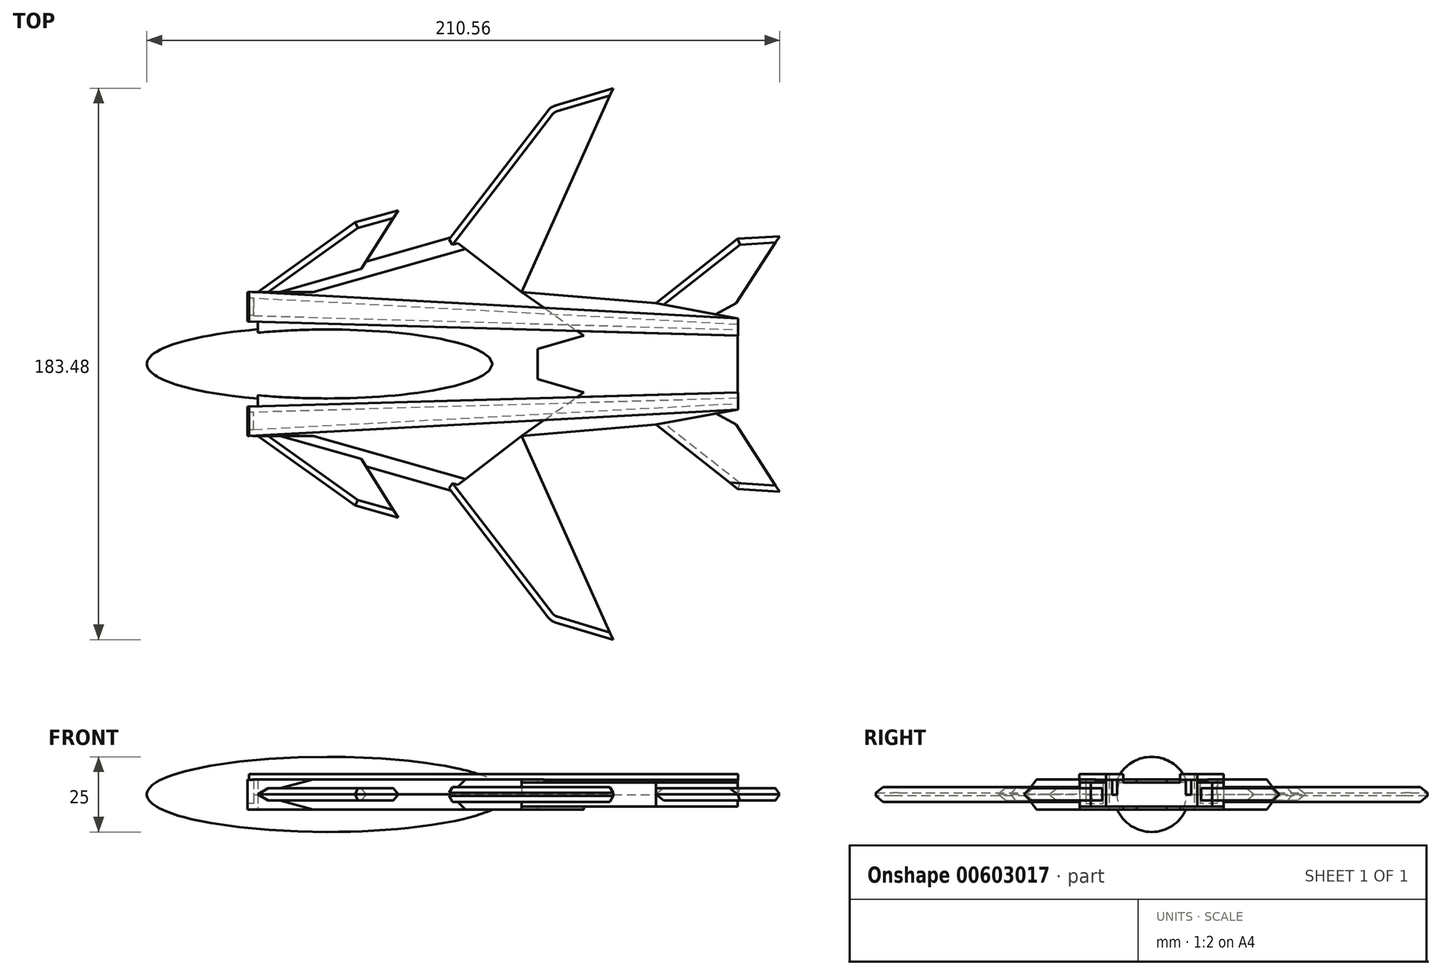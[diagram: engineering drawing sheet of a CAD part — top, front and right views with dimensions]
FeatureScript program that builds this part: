
annotation { "Feature Type Name" : "Feature", "Feature Type Description" : "" }
export const myFeature = defineFeature(function(context is Context, id is Id, definition is map)
    precondition{}
    {
        {
            var Q0;
            Q0=qCreatedBy(makeId("Top.planeOp"),FACE);
            var sketch = newSketch(context, id + "F0", { "sketchPlane" : qUnion([Q0])});
            skEllipticalArc(sketch, "E0", {});
            skLineSegment(sketch, "E1", {"start": v(0, 12.5) * mm, "end": v(0, -12.5) * mm});
            skLineSegment(sketch, "E2", {"start": v(0, 0) * mm, "end": v(-60, 0) * mm});
            const initialGuessF0  = {"E0": [0, 0, 1, 0, 0.06, 0.0125, 3.141592653589793, 4.71238898038469]};
            skSetInitialGuess(sketch, initialGuessF0);
            skSolve(sketch);
        }
        {
            var Q0;
            Q0=qCreatedBy(makeId("Right.planeOp"),FACE);
            var sketch = newSketch(context, id + "F1", { "sketchPlane" : qUnion([Q0])});
            skPoint(sketch, "E3.0", {"position": v(0, 0) * mm});
            skLineSegment(sketch, "E4", {"start": v(0, 0) * mm, "end": v(-12.5, 0) * mm});
            skCircle(sketch, "E5", {"center": v(0, 0) * mm, "radius": 12.5 * mm});
            skSolve(sketch);
        }
        {
            var Q0;
            {var subQ0=sQuery(id+"F0.wireOp",EDGE,"E0");Q0=makeQuery(id+"F0.imprint","IMPRINT",FACE,{"disambiguationData":[TD([[makeQuery(id+"F0.imprint","IMPRINT",EDGE,{"derivedFrom":subQ0}),1.0]])]});}
            var Q1;
            Q1=sQuery(id+"F1.wireOp",EDGE,"E5");
            sweep(context, id + "F2", {"profiles" : qUnion([Q0]), "path" : qUnion([Q1])});
        }
        {
            var Q0;
            Q0=makeQuery(id+"F2.opSweep","SWEPT_BODY",BODY,{"disambiguationData":[OSD([sQuery(id+"F0.wireOp",EDGE,"E0"),sQuery(id+"F0.wireOp",EDGE,"E1"),sQuery(id+"F0.wireOp",EDGE,"E2"),sQuery(id+"F1.wireOp",EDGE,"E5")])]});
            var Q1;
            Q1=qCreatedBy(makeId("Right.planeOp"),FACE);
            mirror(context, id + "F3", {"operationType" : NewBodyOperationType.ADD, "entities" : qUnion([Q0]), "mirrorPlane" : qUnion([Q1])});
        }
        {
            var Q0;
            Q0=qCreatedBy(makeId("Top.planeOp"),FACE);
            var sketch = newSketch(context, id + "F4", { "sketchPlane" : qUnion([Q0])});
            skEllipticalArc(sketch, "E6.0", {});
            skLineSegment(sketch, "E7", {"start": v(-23.05, -11.54) * mm, "end": v(-23.05, -14.14) * mm});
            skLineSegment(sketch, "E8", {"start": v(-23.05, -14.14) * mm, "end": v(-26.5, -14.14) * mm});
            skLineSegment(sketch, "E9", {"start": v(-26.5, -14.14) * mm, "end": v(-26.5, -23.94) * mm});
            skLineSegment(sketch, "E10", {"start": v(-26.5, -23.94) * mm, "end": v(-23.05, -23.94) * mm});
            skLineSegment(sketch, "E11", {"start": v(-23.05, -23.94) * mm, "end": v(41.04, -42.09) * mm});
            skLineSegment(sketch, "E12", {"start": v(41.04, -42.09) * mm, "end": v(64.69, -23.94) * mm});
            skLineSegment(sketch, "E13", {"start": v(64.69, -23.94) * mm, "end": v(85.37, -9.43) * mm});
            skLineSegment(sketch, "E14", {"start": v(85.37, -9.43) * mm, "end": v(70, -5) * mm});
            skLineSegment(sketch, "E15", {"start": v(70, -5) * mm, "end": v(70, 0) * mm});
            skLineSegment(sketch, "E16", {"start": v(-23.05, -23.94) * mm, "end": v(9.37, -47.1) * mm});
            skLineSegment(sketch, "E17", {"start": v(9.37, -47.1) * mm, "end": v(23.65, -51.15) * mm});
            skLineSegment(sketch, "E18", {"start": v(23.65, -51.15) * mm, "end": v(12.96, -34.14) * mm});
            skLineSegment(sketch, "E19", {"start": v(64.69, -23.94) * mm, "end": v(109.34, -20.2) * mm});
            skLineSegment(sketch, "E20", {"start": v(109.34, -20.2) * mm, "end": v(136.64, -15.13) * mm});
            skLineSegment(sketch, "E21", {"start": v(136.64, -15.13) * mm, "end": v(136.64, 0) * mm});
            skLineSegment(sketch, "E22", {"start": v(136.64, 0) * mm, "end": v(70, 0) * mm});
            skLineSegment(sketch, "E23", {"start": v(109.34, -20.2) * mm, "end": v(136.64, -41.65) * mm});
            skLineSegment(sketch, "E24", {"start": v(136.64, -41.65) * mm, "end": v(150.56, -42.52) * mm});
            skLineSegment(sketch, "E25", {"start": v(150.56, -42.52) * mm, "end": v(136.06, -20.2) * mm});
            skLineSegment(sketch, "E26", {"start": v(136.06, -20.2) * mm, "end": v(129.3, -16.5) * mm});
            skLineSegment(sketch, "E27", {"start": v(-23.05, -11.54) * mm, "end": v(-23.05, 0) * mm});
            skLineSegment(sketch, "E28", {"start": v(-23.05, 0) * mm, "end": v(70, 0) * mm});
            skLineSegment(sketch, "E29", {"start": v(41.04, -42.09) * mm, "end": v(73.42, -84.26) * mm});
            skLineSegment(sketch, "E30", {"start": v(75.95, -86) * mm, "end": v(95.11, -91.74) * mm});
            skLineSegment(sketch, "E31", {"start": v(95.11, -91.74) * mm, "end": v(64.69, -23.94) * mm});
            skPoint(sketch, "E32.visualSharp", {"position": v(74.4, -85.54) * mm});
            skArc(sketch, "E32.filletArc", {"start": v(73.42, -84.26) * mm, "mid": v(74.55, -85.33) * mm, "end": v(75.95, -86) * mm});
            const initialGuessF4  = {"E6.0": [0, 0, 1, 0, 0.06, 0.0125, 3.141592653589793, 4.71238898038469]};
            skSetInitialGuess(sketch, initialGuessF4);
            skSolve(sketch);
        }
        {
            var Q0;
            Q0=makeQuery(id+"F4.imprint","IMPRINT",FACE,{"disambiguationData":[TD([[makeQuery(id+"F4.imprint","IMPRINT",EDGE,{"derivedFrom":sQuery(id+"F4.wireOp",EDGE,"E7")}),1.0]])]});
            extrude(context, id + "F5", {"entities" : qUnion([Q0]), "operationType" : NewBodyOperationType.ADD, "endBound" : BoundingType.SYMMETRIC, "depth" : 10 * mm, "offsetDistance" : 25 * mm});
        }
        {
            var Q0;
            Q0=makeQuery(id+"F4.imprint","IMPRINT",FACE,{"disambiguationData":[TD([[makeQuery(id+"F4.imprint","IMPRINT",EDGE,{"derivedFrom":sQuery(id+"F4.wireOp",EDGE,"E13")}),-1.0]])]});
            extrude(context, id + "F6", {"entities" : qUnion([Q0]), "operationType" : NewBodyOperationType.ADD, "endBound" : BoundingType.SYMMETRIC, "depth" : 8 * mm, "offsetDistance" : 25 * mm});
        }
        {
            var Q0;
            {var subQ0=sQuery(id+"F4.wireOp",EDGE,"E16");Q0=makeQuery(id+"F4.imprint","IMPRINT",FACE,{"disambiguationData":[TD([[makeQuery(id+"F4.imprint","IMPRINT",EDGE,{"derivedFrom":subQ0}),1.0]])]});}
            var Q1;
            {var subQ0=sQuery(id+"F4.wireOp",EDGE,"E23");Q1=makeQuery(id+"F4.imprint","IMPRINT",FACE,{"disambiguationData":[TD([[makeQuery(id+"F4.imprint","IMPRINT",EDGE,{"derivedFrom":subQ0}),1.0]])]});}
            extrude(context, id + "F7", {"entities" : qUnion([Q0, Q1]), "operationType" : NewBodyOperationType.ADD, "endBound" : BoundingType.SYMMETRIC, "depth" : 4 * mm, "offsetDistance" : 25 * mm});
        }
        {
            var Q0;
            Q0=makeQuery(id+"F5.opExtrude","CAP_FACE",FACE,{"disambiguationData":[OSD([sQuery(id+"F4.wireOp",EDGE,"E7"),sQuery(id+"F4.wireOp",EDGE,"E8"),sQuery(id+"F4.wireOp",EDGE,"E9"),sQuery(id+"F4.wireOp",EDGE,"E10"),sQuery(id+"F4.wireOp",EDGE,"E11"),sQuery(id+"F4.wireOp",EDGE,"E12"),sQuery(id+"F4.wireOp",EDGE,"E13"),sQuery(id+"F4.wireOp",EDGE,"E14"),sQuery(id+"F4.wireOp",EDGE,"E15"),sQuery(id+"F4.wireOp",EDGE,"E27"),sQuery(id+"F4.wireOp",EDGE,"E28")])],"isStart":false});
            var sketch = newSketch(context, id + "F8", { "sketchPlane" : qUnion([Q0])});
            skLineSegment(sketch, "E33.0.0", {"start": v(136.64, -15.13) * mm, "end": v(136.64, 0) * mm});
            skLineSegment(sketch, "E33.0.1", {"start": v(136.64, 0) * mm, "end": v(70, 0) * mm});
            skLineSegment(sketch, "E33.0.2", {"start": v(70, 0) * mm, "end": v(70, -5) * mm});
            skLineSegment(sketch, "E33.0.3", {"start": v(70, -5) * mm, "end": v(85.37, -9.43) * mm});
            skLineSegment(sketch, "E33.0.4", {"start": v(85.37, -9.43) * mm, "end": v(64.69, -23.94) * mm});
            skLineSegment(sketch, "E33.0.5", {"start": v(64.69, -23.94) * mm, "end": v(109.34, -20.2) * mm});
            skLineSegment(sketch, "E33.0.6", {"start": v(109.34, -20.2) * mm, "end": v(136.64, -15.13) * mm});
            skLineSegment(sketch, "E34", {"start": v(136.64, -15.13) * mm, "end": v(-26.5, -23.94) * mm});
            skLineSegment(sketch, "E35", {"start": v(-26.5, -23.94) * mm, "end": v(-26.5, -14.14) * mm});
            skLineSegment(sketch, "E36", {"start": v(-26.5, -14.14) * mm, "end": v(136.64, -9.43) * mm});
            skLineSegment(sketch, "E37", {"start": v(136.64, -9.43) * mm, "end": v(136.64, -15.13) * mm});
            skLineSegment(sketch, "E38.0", {"start": v(-24.5, -16.08) * mm, "end": v(136.64, -11.44) * mm});
            skLineSegment(sketch, "E38.1", {"start": v(-24.5, -21.83) * mm, "end": v(-24.5, -16.08) * mm});
            skLineSegment(sketch, "E38.2", {"start": v(136.64, -13.13) * mm, "end": v(-24.5, -21.83) * mm});
            skSolve(sketch);
        }
        {
            var Q0;
            {var subQ0=sQuery(id+"F8.wireOp",EDGE,"E35");Q0=makeQuery(id+"F8.imprint","IMPRINT",FACE,{"disambiguationData":[TD([[makeQuery(id+"F8.imprint","IMPRINT",EDGE,{"derivedFrom":subQ0}),1.0]])]});}
            var Q1;
            {var subQ0=sQuery(id+"F8.wireOp",EDGE,"E34");var subQ1=sQuery(id+"F8.wireOp",EDGE,"E33.0.4");var subQ2=makeQuery(id+"F8.imprint","INTERSECT",VERTEX,{"derivedFrom":[subQ1,subQ0]});Q1=makeQuery(id+"F8.imprint","IMPRINT",FACE,{"disambiguationData":[TD([[makeQuery(id+"F8.imprint","IMPRINT",EDGE,{"disambiguationData":[TD([[subQ2,-1.0]])],"derivedFrom":subQ1}),-1.0]])]});}
            var Q2;
            {var subQ0=sQuery(id+"F8.wireOp",EDGE,"E38.0");var subQ1=sQuery(id+"F8.wireOp",EDGE,"E33.0.4");var subQ2=makeQuery(id+"F8.imprint","INTERSECT",VERTEX,{"derivedFrom":[subQ1,subQ0]});Q2=makeQuery(id+"F8.imprint","IMPRINT",FACE,{"disambiguationData":[TD([[makeQuery(id+"F8.imprint","IMPRINT",EDGE,{"disambiguationData":[TD([[subQ2,-1.0]])],"derivedFrom":subQ1}),-1.0]])]});}
            extrude(context, id + "F9", {"entities" : qUnion([Q0, Q1, Q2]), "operationType" : NewBodyOperationType.ADD, "oppositeDirection" : true, "depth" : 4 * mm, "offsetDistance" : 25 * mm});
        }
        {
            var Q0;
            {var subQ5=sQuery(id+"F8.wireOp",EDGE,"E38.1");Q0=makeQuery(id+"F8.imprint","IMPRINT",FACE,{"disambiguationData":[TD([[makeQuery(id+"F8.imprint","IMPRINT",EDGE,{"derivedFrom":subQ5}),-1.0]])]});}
            var Q1;
            {var subQ0=sQuery(id+"F8.wireOp",EDGE,"E38.2");var subQ1=sQuery(id+"F8.wireOp",EDGE,"E33.0.4");var subQ2=makeQuery(id+"F8.imprint","INTERSECT",VERTEX,{"derivedFrom":[subQ1,subQ0]});Q1=makeQuery(id+"F8.imprint","IMPRINT",FACE,{"disambiguationData":[TD([[makeQuery(id+"F8.imprint","IMPRINT",EDGE,{"disambiguationData":[TD([[subQ2,-1.0]])],"derivedFrom":subQ1}),-1.0]])]});}
            extrude(context, id + "F10", {"entities" : qUnion([Q0, Q1]), "operationType" : NewBodyOperationType.REMOVE, "oppositeDirection" : true, "depth" : 5.1 * mm, "offsetDistance" : 25 * mm});
        }
        {
            var Q0;
            Q0=makeQuery(id+"F5.opExtrude","SWEPT_FACE",FACE,{"disambiguationData":[OSD([sQuery(id+"F4.wireOp",EDGE,"E9")])]});
            var sketch = newSketch(context, id + "F11", { "sketchPlane" : qUnion([Q0])});
            skLineSegment(sketch, "E39.bottom", {"start": v(21.94, 5) * mm, "end": v(16.14, 5) * mm});
            skLineSegment(sketch, "E39.top", {"start": v(21.94, -3) * mm, "end": v(16.14, -3) * mm});
            skLineSegment(sketch, "E39.left", {"start": v(21.94, 5) * mm, "end": v(21.94, -3) * mm});
            skLineSegment(sketch, "E39.right", {"start": v(16.14, 5) * mm, "end": v(16.14, -3) * mm});
            skLineSegment(sketch, "E40.bottom", {"start": v(16.14, -3) * mm, "end": v(16.14, -3) * mm});
            skSolve(sketch);
        }
        {
            var Q0;
            Q0=qCreatedBy(makeId("Top.planeOp"),FACE);
            cPlane(context, id + "F12", {"entities" : qUnion([Q0]), "cplaneType" : CPlaneType.OFFSET, "offset" : 4.8 * mm, "width" : 150 * mm, "height" : 150 * mm});
        }
        {
            var Q0;
            Q0=qCreatedBy(id+"F12.planeOp",FACE);
            var sketch = newSketch(context, id + "F13", { "sketchPlane" : qUnion([Q0])});
            skLineSegment(sketch, "E41", {"start": v(-26, -14.12) * mm, "end": v(-26, -24) * mm});
            skLineSegment(sketch, "E42", {"start": v(-26, -24) * mm, "end": v(136.68, -15.15) * mm});
            skLineSegment(sketch, "E43", {"start": v(136.68, -15.15) * mm, "end": v(136.68, -9.47) * mm});
            skLineSegment(sketch, "E44", {"start": v(136.68, -9.47) * mm, "end": v(-26, -14.12) * mm});
            skSolve(sketch);
        }
        {
            var Q0;
            Q0 = qSketchRegion(id + "F13", true);
            var Q1;
            Q1=makeQuery(id+"F13.imprint","IMPRINT",FACE,{"disambiguationData":[TD([[makeQuery(id+"F13.imprint","IMPRINT",EDGE,{"derivedFrom":sQuery(id+"F13.wireOp",EDGE,"E41")}),1.0]])]});
            extrude(context, id + "F14", {"entities" : qUnion([Q0, Q1]), "operationType" : NewBodyOperationType.ADD, "depth" : 2 * mm, "offsetDistance" : 25 * mm});
        }
        {
            var Q0;
            Q0=makeQuery(id+"F11.imprint","IMPRINT",FACE,{"disambiguationData":[TD([[makeQuery(id+"F11.imprint","IMPRINT",EDGE,{"derivedFrom":sQuery(id+"F11.wireOp",EDGE,"E39.bottom")}),-1.0]])]});
            extrude(context, id + "F15", {"entities" : qUnion([Q0]), "operationType" : NewBodyOperationType.REMOVE, "oppositeDirection" : true, "depth" : 2 * mm, "offsetDistance" : 25 * mm});
        }
        {
            var Q0;
            Q0=makeQuery(id+"F2.opSweep","SWEPT_BODY",BODY,{"disambiguationData":[OSD([sQuery(id+"F0.wireOp",EDGE,"E0"),sQuery(id+"F0.wireOp",EDGE,"E1"),sQuery(id+"F0.wireOp",EDGE,"E2"),sQuery(id+"F1.wireOp",EDGE,"E5")])]});
            var Q1;
            Q1=qCreatedBy(makeId("Front.planeOp"),FACE);
            mirror(context, id + "F16", {"operationType" : NewBodyOperationType.ADD, "entities" : qUnion([Q0]), "mirrorPlane" : qUnion([Q1])});
        }
        {
            var Q0;
            Q0=makeQuery(id+"F4.imprint","IMPRINT",FACE,{"disambiguationData":[TD([[makeQuery(id+"F4.imprint","IMPRINT",EDGE,{"derivedFrom":sQuery(id+"F4.wireOp",EDGE,"E12")}),-1.0]])]});
            extrude(context, id + "F17", {"entities" : qUnion([Q0]), "operationType" : NewBodyOperationType.ADD, "endBound" : BoundingType.SYMMETRIC, "depth" : 5 * mm, "offsetDistance" : 25 * mm});
        }
        {
            var Q0;
            Q0=makeQuery(id+"F2.opSweep","SWEPT_BODY",BODY,{"disambiguationData":[OSD([sQuery(id+"F0.wireOp",EDGE,"E0"),sQuery(id+"F0.wireOp",EDGE,"E1"),sQuery(id+"F0.wireOp",EDGE,"E2"),sQuery(id+"F1.wireOp",EDGE,"E5")])]});
            var Q1;
            Q1=qCreatedBy(makeId("Front.planeOp"),FACE);
            mirror(context, id + "F18", {"operationType" : NewBodyOperationType.ADD, "entities" : qUnion([Q0]), "mirrorPlane" : qUnion([Q1])});
        }
        {
            var Q0;
            Q0=makeQuery(id+"F5.opExtrude","CAP_EDGE",EDGE,{"disambiguationData":[OSD([sQuery(id+"F4.wireOp",EDGE,"E11")])],"isStart":true});
            var Q1;
            Q1=makeQuery(id+"F5.opExtrude","CAP_EDGE",EDGE,{"disambiguationData":[OSD([sQuery(id+"F4.wireOp",EDGE,"E11")])],"isStart":false});
            var Q2;
            Q2=makeQuery(id+"F16.opPattern","COPY",EDGE,{"derivedFrom":makeQuery(id+"F5.opExtrude","CAP_EDGE",EDGE,{"disambiguationData":[OSD([sQuery(id+"F4.wireOp",EDGE,"E11")])],"isStart":false}),"instanceName":"1"});
            var Q3;
            Q3=makeQuery(id+"F16.opPattern","COPY",EDGE,{"derivedFrom":makeQuery(id+"F5.opExtrude","CAP_EDGE",EDGE,{"disambiguationData":[OSD([sQuery(id+"F4.wireOp",EDGE,"E11")])],"isStart":true}),"instanceName":"1"});
            chamfer(context, id + "F19", {"entities" : qUnion([Q0, Q1, Q2, Q3]), "width" : 5 * mm, "tangentPropagation" : true});
        }
        {
            var Q0;
            Q0=makeQuery(id+"F7.opExtrude","CAP_EDGE",EDGE,{"disambiguationData":[OSD([sQuery(id+"F4.wireOp",EDGE,"E16")])],"isStart":false});
            var Q1;
            Q1=makeQuery(id+"F7.opExtrude","CAP_EDGE",EDGE,{"disambiguationData":[OSD([sQuery(id+"F4.wireOp",EDGE,"E16")])],"isStart":true});
            var Q2;
            Q2=makeQuery(id+"F7.opExtrude","CAP_EDGE",EDGE,{"disambiguationData":[OSD([sQuery(id+"F4.wireOp",EDGE,"E17")])],"isStart":true});
            var Q3;
            Q3=makeQuery(id+"F7.opExtrude","CAP_EDGE",EDGE,{"disambiguationData":[OSD([sQuery(id+"F4.wireOp",EDGE,"E17")])],"isStart":false});
            var Q4;
            Q4=makeQuery(id+"F17.opExtrude","CAP_EDGE",EDGE,{"disambiguationData":[OSD([sQuery(id+"F4.wireOp",EDGE,"E29")])],"isStart":false});
            var Q5;
            Q5=makeQuery(id+"F17.opExtrude","CAP_EDGE",EDGE,{"disambiguationData":[OSD([sQuery(id+"F4.wireOp",EDGE,"E29")])],"isStart":true});
            var Q6;
            Q6=makeQuery(id+"F7.opExtrude","CAP_EDGE",EDGE,{"disambiguationData":[OSD([sQuery(id+"F4.wireOp",EDGE,"E23")])],"isStart":true});
            var Q7;
            Q7=makeQuery(id+"F7.opExtrude","CAP_EDGE",EDGE,{"disambiguationData":[OSD([sQuery(id+"F4.wireOp",EDGE,"E24")])],"isStart":false});
            var Q8;
            Q8=makeQuery(id+"F7.opExtrude","CAP_EDGE",EDGE,{"disambiguationData":[OSD([sQuery(id+"F4.wireOp",EDGE,"E24")])],"isStart":true});
            var Q9;
            Q9=makeQuery(id+"F18.opPattern","COPY",EDGE,{"derivedFrom":makeQuery(id+"F17.opExtrude","CAP_EDGE",EDGE,{"disambiguationData":[OSD([sQuery(id+"F4.wireOp",EDGE,"E29")])],"isStart":false}),"instanceName":"1"});
            var Q10;
            Q10=makeQuery(id+"F18.opPattern","COPY",EDGE,{"derivedFrom":makeQuery(id+"F17.opExtrude","CAP_EDGE",EDGE,{"disambiguationData":[OSD([sQuery(id+"F4.wireOp",EDGE,"E29")])],"isStart":true}),"instanceName":"1"});
            var Q11;
            Q11=makeQuery(id+"F16.opPattern","COPY",EDGE,{"derivedFrom":makeQuery(id+"F7.opExtrude","CAP_EDGE",EDGE,{"disambiguationData":[OSD([sQuery(id+"F4.wireOp",EDGE,"E17")])],"isStart":false}),"instanceName":"1"});
            var Q12;
            Q12=makeQuery(id+"F16.opPattern","COPY",EDGE,{"derivedFrom":makeQuery(id+"F7.opExtrude","CAP_EDGE",EDGE,{"disambiguationData":[OSD([sQuery(id+"F4.wireOp",EDGE,"E17")])],"isStart":true}),"instanceName":"1"});
            var Q13;
            Q13=makeQuery(id+"F16.opPattern","COPY",EDGE,{"derivedFrom":makeQuery(id+"F7.opExtrude","CAP_EDGE",EDGE,{"disambiguationData":[OSD([sQuery(id+"F4.wireOp",EDGE,"E16")])],"isStart":true}),"instanceName":"1"});
            var Q14;
            Q14=makeQuery(id+"F16.opPattern","COPY",EDGE,{"derivedFrom":makeQuery(id+"F7.opExtrude","CAP_EDGE",EDGE,{"disambiguationData":[OSD([sQuery(id+"F4.wireOp",EDGE,"E16")])],"isStart":false}),"instanceName":"1"});
            var Q15;
            Q15=makeQuery(id+"F16.opPattern","COPY",EDGE,{"derivedFrom":makeQuery(id+"F7.opExtrude","CAP_EDGE",EDGE,{"disambiguationData":[OSD([sQuery(id+"F4.wireOp",EDGE,"E24")])],"isStart":false}),"instanceName":"1"});
            var Q16;
            Q16=makeQuery(id+"F16.opPattern","COPY",EDGE,{"derivedFrom":makeQuery(id+"F7.opExtrude","CAP_EDGE",EDGE,{"disambiguationData":[OSD([sQuery(id+"F4.wireOp",EDGE,"E24")])],"isStart":true}),"instanceName":"1"});
            var Q17;
            Q17=makeQuery(id+"F16.opPattern","COPY",EDGE,{"derivedFrom":makeQuery(id+"F7.opExtrude","CAP_EDGE",EDGE,{"disambiguationData":[OSD([sQuery(id+"F4.wireOp",EDGE,"E23")])],"isStart":true}),"instanceName":"1"});
            var Q18;
            Q18=makeQuery(id+"F16.opPattern","COPY",EDGE,{"derivedFrom":makeQuery(id+"F7.opExtrude","CAP_EDGE",EDGE,{"disambiguationData":[OSD([sQuery(id+"F4.wireOp",EDGE,"E23")])],"isStart":false}),"instanceName":"1"});
            chamfer(context, id + "F20", {"entities" : qUnion([Q0, Q1, Q2, Q3, Q4, Q5, Q6, Q7, Q8, Q9, Q10, Q11, Q12, Q13, Q14, Q15, Q16, Q17, Q18]), "width" : 2 * mm, "tangentPropagation" : true});
        }
    });
